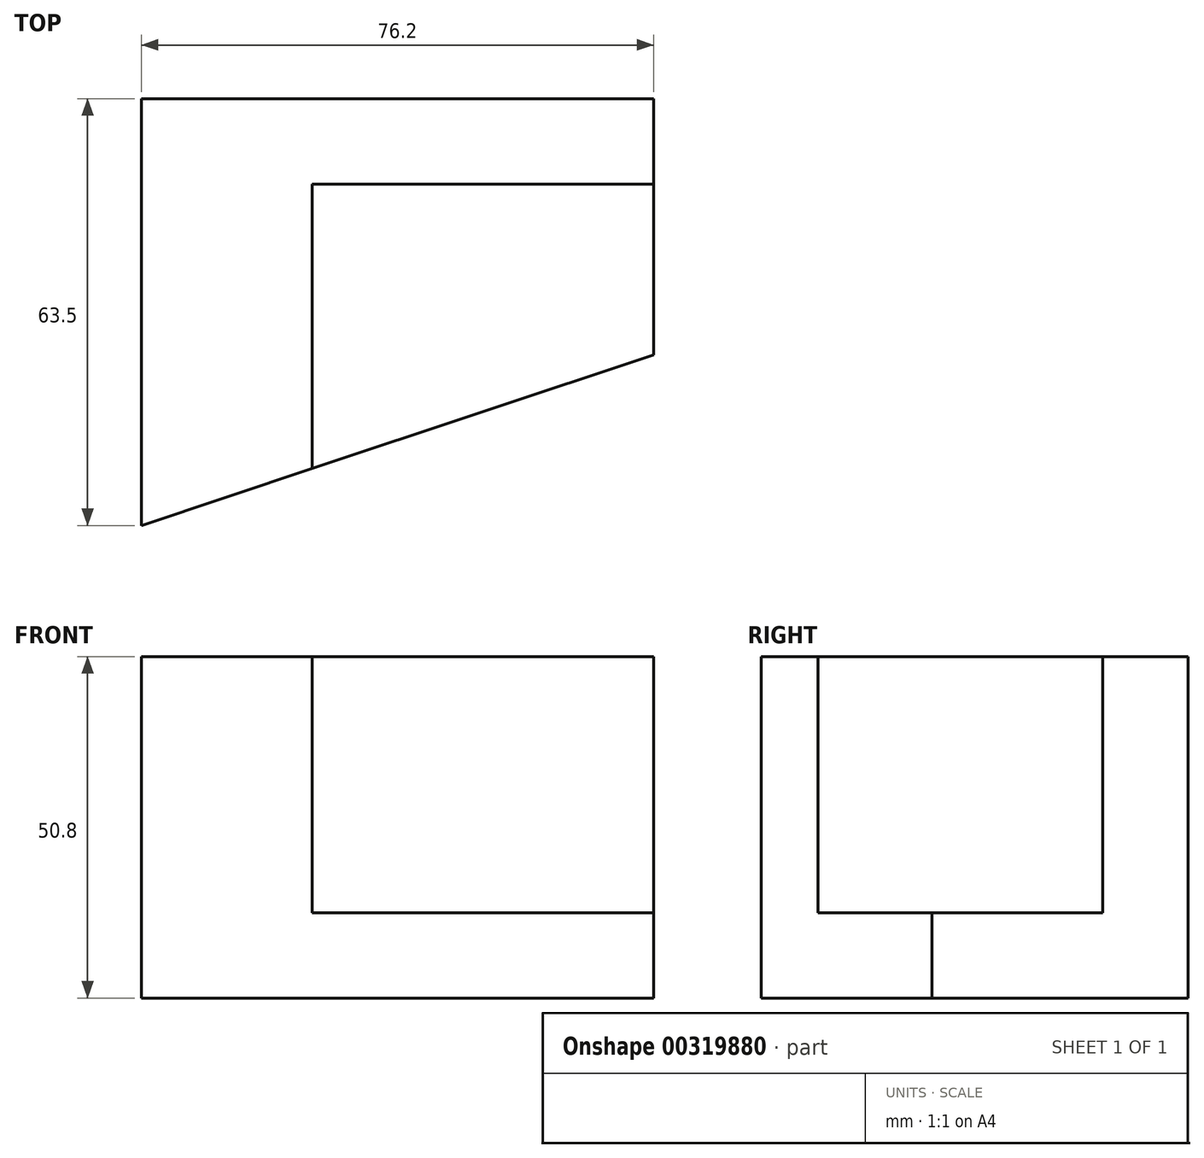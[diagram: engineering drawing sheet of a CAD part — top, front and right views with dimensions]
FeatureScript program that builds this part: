
annotation { "Feature Type Name" : "Feature", "Feature Type Description" : "" }
export const myFeature = defineFeature(function(context is Context, id is Id, definition is map)
    precondition{}
    {
        {
            var Q0;
            Q0=qCreatedBy(makeId("Top.planeOp"),FACE);
            var sketch = newSketch(context, id + "F0", { "sketchPlane" : qUnion([Q0])});
            skLineSegment(sketch, "E0", {"start": v(0, 0) * mm, "end": v(0, 63.5) * mm});
            skLineSegment(sketch, "E1", {"start": v(0, 63.5) * mm, "end": v(76.2, 63.5) * mm});
            skLineSegment(sketch, "E2", {"start": v(76.2, 63.5) * mm, "end": v(76.2, 25.4) * mm});
            skLineSegment(sketch, "E3", {"start": v(76.2, 25.4) * mm, "end": v(0, 0) * mm});
            skLineSegment(sketch, "E4", {"start": v(76.2, 63.5) * mm, "end": v(76.2, 50.8) * mm});
            skLineSegment(sketch, "E5", {"start": v(76.2, 50.8) * mm, "end": v(25.4, 50.8) * mm});
            skLineSegment(sketch, "E6", {"start": v(25.4, 50.8) * mm, "end": v(25.4, 8.47) * mm});
            skSolve(sketch);
        }
        {
            var Q0;
            {var subQ1=sQuery(id+"F0.wireOp",EDGE,"E0");Q0=makeQuery(id+"F0.imprint","IMPRINT",FACE,{"disambiguationData":[TD([[makeQuery(id+"F0.imprint","IMPRINT",EDGE,{"derivedFrom":subQ1}),-1.0]])]});}
            extrude(context, id + "F1", {"entities" : qUnion([Q0]), "depth" : 50.8 * mm});
        }
        {
            var Q0;
            {var subQ0=sQuery(id+"F0.wireOp",EDGE,"E2");Q0=makeQuery(id+"F0.imprint","IMPRINT",FACE,{"disambiguationData":[TD([[makeQuery(id+"F0.imprint","IMPRINT",EDGE,{"derivedFrom":subQ0}),-1.0]])]});}
            extrude(context, id + "F2", {"entities" : qUnion([Q0]), "operationType" : NewBodyOperationType.ADD, "depth" : 12.7 * mm});
        }
    });
